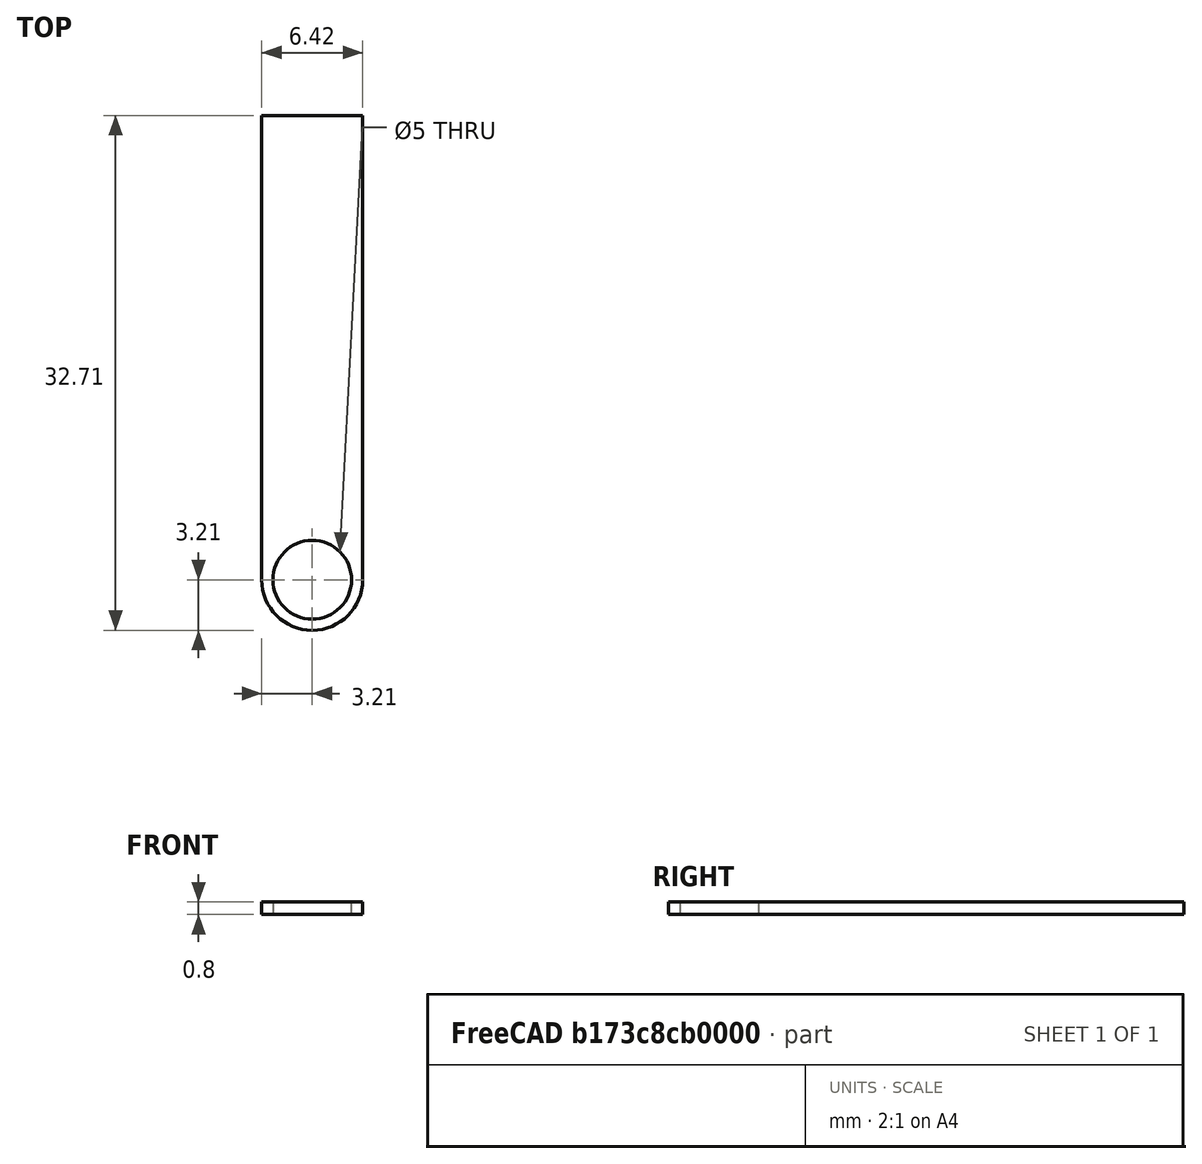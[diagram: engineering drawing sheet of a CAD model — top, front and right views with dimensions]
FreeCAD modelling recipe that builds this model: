
FCSTD DOCUMENT  (FreeCAD 0.20R29177 +233 (Git))
Label: E_Sensor_plate
License: All rights reserved
LicenseURL: http://en.wikipedia.org/wiki/All_rights_reserved
objects: Sketcher::SketchObject×1, PartDesign::Pad×1, PartDesign::Body×1
note: 4 computed .brp shape members not serialized (recipe doc carries the construction recipe); baked Part::Feature solids carry a one-line shape summary decoded from their .brp

FEATURE [Sketcher::SketchObject] Sketch
  FullyConstrained = false
  MapMode = 5
  Support = -> [XY_Plane]
  sketch-geometry (5):
    g0: Circle CenterX=0 CenterY=0 CenterZ=0 NormalX=0 NormalY=0 NormalZ=1 AngleXU=0 Radius=2.5
    g1: ArcOfCircle CenterX=0 CenterY=0 CenterZ=0 NormalX=0 NormalY=0 NormalZ=1 AngleXU=0 Radius=3.20733 StartAngle=3.14159 EndAngle=6.28319
    g2: LineSegment StartX=3.20733 StartY=-8e-16 StartZ=0 EndX=3.20733 EndY=29.5 EndZ=0
    g3: LineSegment StartX=-3.20733 StartY=4e-16 StartZ=0 EndX=-3.20733 EndY=29.5 EndZ=0
    g4: LineSegment StartX=-3.20733 StartY=29.5 StartZ=0 EndX=3.20733 EndY=29.5 EndZ=0
  constraints (13):
    c: Coincident(g0,g-1)
    c: Diameter(g0) = 5
    c: Coincident(g1,g0)
    c: PointOnObject(g1,g-1)
    c: PointOnObject(g1,g-1)
    c: Coincident(g2,g1)
    c: Vertical(g2)
    c: Distance(g2) = 29.5
    c: Coincident(g3,g1)
    c: Vertical(g3)
    c: Distance(g3) = 29.5
    c: Coincident(g4,g3)
    c: Coincident(g4,g2)
FEATURE [PartDesign::Pad] Pad
  Direction = (0,0,1)
  Length = 0.8
  Length2 = 10
  Profile = -> Sketch
  ReferenceAxis = -> Sketch [N_Axis]
  Type = 0
FEATURE [PartDesign::Body] Body
  Group = -> [Sketch,Pad]
  Origin = -> Origin
  Tip = -> Pad
